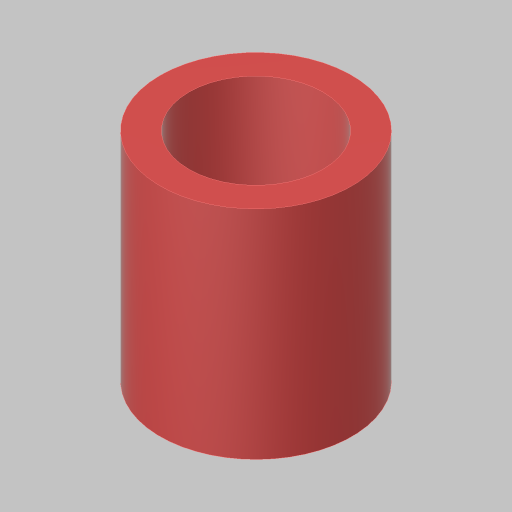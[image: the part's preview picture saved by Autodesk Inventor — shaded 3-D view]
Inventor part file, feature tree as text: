
AUTODESK INVENTOR PART (.ipt)
format: ipt  version: 2023.5 (Build 275446000, 446)  size: 105,472 bytes
history: native  units: in
note: dims shown in document units (in); Inventor stores cm internally (conversion verified against a paired STEP export)
features: extrude x1, sketch x1
ambient origin geometry x8: Origin, YZ Plane, XZ Plane, XY Plane, X Axis, Y Axis, Z Axis, Center Point
bodies: Solid1 (feature_tree)
feature tree (2):
  extrude  "Extrusion1"  Depth=0.94in
  sketch  "Sketch1"  dims[d0=0.58in d1=0.125in d2=0.94in d3=0.0in]
